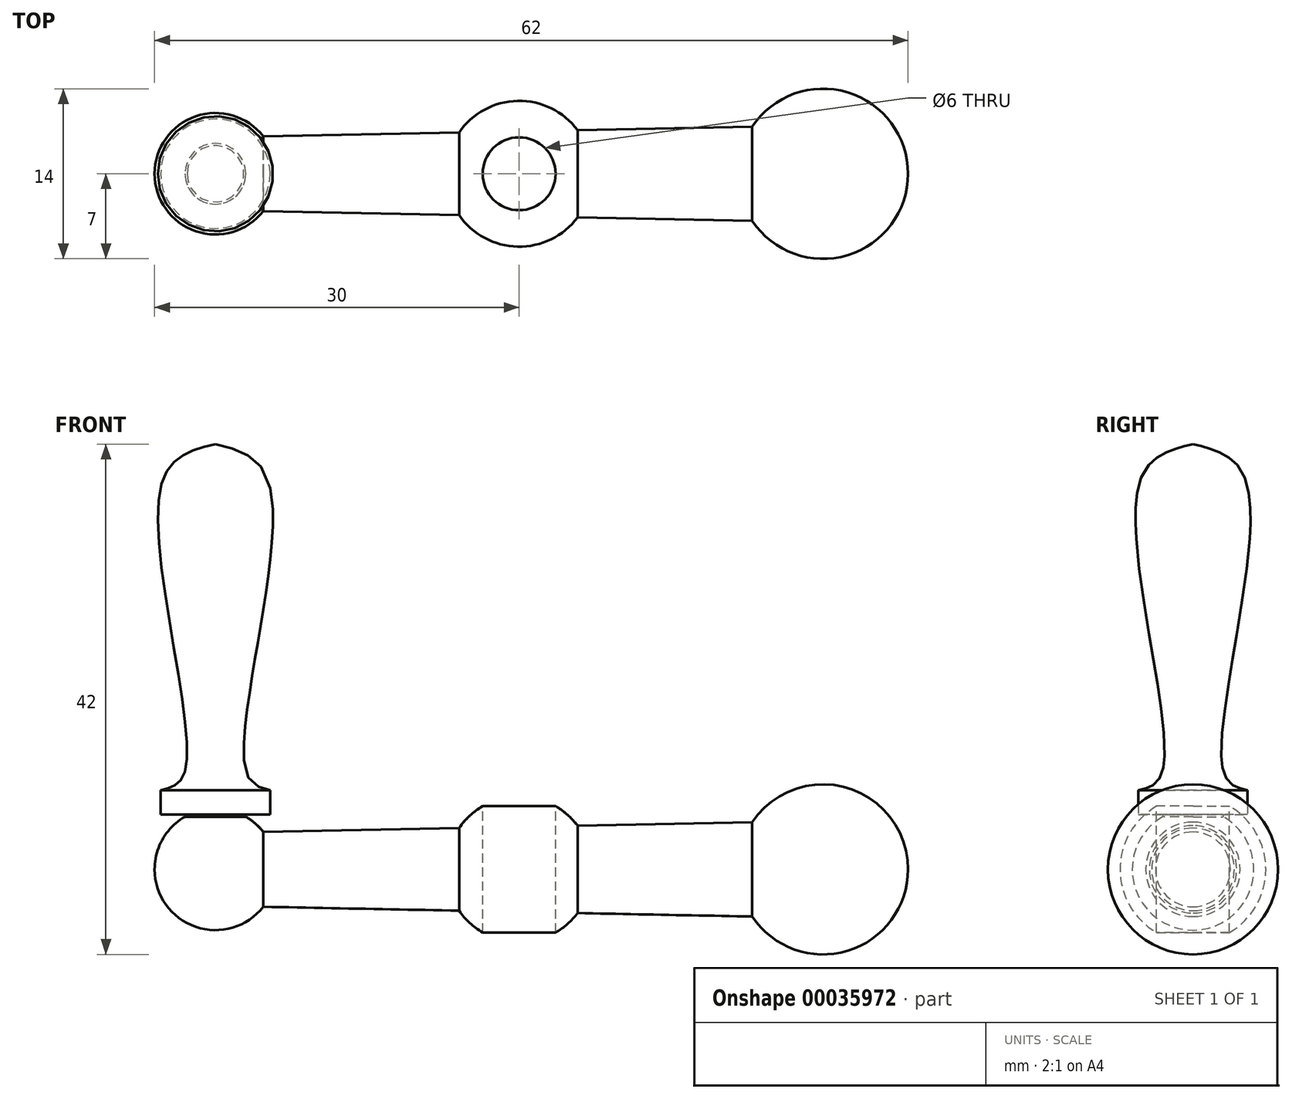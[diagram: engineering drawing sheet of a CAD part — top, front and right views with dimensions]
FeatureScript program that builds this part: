
annotation { "Feature Type Name" : "Feature", "Feature Type Description" : "" }
export const myFeature = defineFeature(function(context is Context, id is Id, definition is map)
    precondition{}
    {
        {
            var Q0;
            Q0=qCreatedBy(makeId("Front.planeOp"),FACE);
            var sketch = newSketch(context, id + "F0", { "sketchPlane" : qUnion([Q0])});
            skArc(sketch, "E0", {"start": v(-6, 0) * mm, "mid": v(0, -6) * mm, "end": v(6, 0) * mm});
            skLineSegment(sketch, "E1", {"start": v(25, 0) * mm, "end": v(0, 0) * mm});
            skLineSegment(sketch, "E2", {"start": v(0, 0) * mm, "end": v(-25, 0) * mm});
            skLineSegment(sketch, "E3", {"start": v(0, 0) * mm, "end": v(25, 0) * mm});
            skArc(sketch, "E4", {"start": v(18, 0) * mm, "mid": v(25, -7) * mm, "end": v(32, 0) * mm});
            skArc(sketch, "E5", {"start": v(-30, 0) * mm, "mid": v(-25, -5) * mm, "end": v(-20, 0) * mm});
            skLineSegment(sketch, "E6", {"start": v(-25, 0) * mm, "end": v(-25, 3) * mm});
            skLineSegment(sketch, "E7", {"start": v(25, 0) * mm, "end": v(25, 4) * mm});
            skLineSegment(sketch, "E8", {"start": v(-25, 3) * mm, "end": v(25, 4) * mm});
            skLineSegment(sketch, "E9", {"start": v(-30, 0) * mm, "end": v(32, 0) * mm});
            skSolve(sketch);
        }
        {
            var Q0;
            {var subQ2=sQuery(id+"F0.wireOp",EDGE,"E6");Q0=makeQuery(id+"F0.imprint","IMPRINT",FACE,{"disambiguationData":[TD([[makeQuery(id+"F0.imprint","IMPRINT",EDGE,{"derivedFrom":subQ2}),-1.0]])]});}
            var Q1;
            Q1=sQuery(id+"F0.wireOp",EDGE,"E9");
            revolve(context, id + "F1", {"entities" : qUnion([Q0]), "axis" : qUnion([Q1]), "revolveType" : RevolveType.FULL});
        }
        {
            var Q0;
            {var subQ0=sQuery(id+"F0.wireOp",EDGE,"E5");Q0=makeQuery(id+"F0.imprint","IMPRINT",FACE,{"disambiguationData":[TD([[makeQuery(id+"F0.imprint","IMPRINT",EDGE,{"derivedFrom":subQ0}),1.0]])]});}
            var Q1;
            {var subQ0=sQuery(id+"F0.wireOp",EDGE,"E0");Q1=makeQuery(id+"F0.imprint","IMPRINT",FACE,{"disambiguationData":[TD([[makeQuery(id+"F0.imprint","IMPRINT",EDGE,{"derivedFrom":subQ0}),1.0]])]});}
            var Q2;
            {var subQ0=sQuery(id+"F0.wireOp",EDGE,"E4");Q2=makeQuery(id+"F0.imprint","IMPRINT",FACE,{"disambiguationData":[TD([[makeQuery(id+"F0.imprint","IMPRINT",EDGE,{"derivedFrom":subQ0}),1.0]])]});}
            var Q3;
            Q3=sQuery(id+"F0.wireOp",EDGE,"E9");
            revolve(context, id + "F2", {"operationType" : NewBodyOperationType.ADD, "entities" : qUnion([Q0, Q1, Q2]), "axis" : qUnion([Q3]), "revolveType" : RevolveType.FULL});
        }
        {
            var Q0;
            Q0=qCreatedBy(makeId("Top.planeOp"),FACE);
            var sketch = newSketch(context, id + "F3", { "sketchPlane" : qUnion([Q0])});
            skCircle(sketch, "E10", {"center": v(0, 0) * mm, "radius": 3 * mm});
            skSolve(sketch);
        }
        {
            var Q0;
            Q0 = qSketchRegion(id + "F3", true);
            extrude(context, id + "F4", {"entities" : qUnion([Q0]), "operationType" : NewBodyOperationType.REMOVE, "oppositeDirection" : true, "depth" : 25 * mm, "hasSecondDirection" : true, "secondDirectionOppositeDirection" : false, "secondDirectionDepth" : 25 * mm});
        }
        {
            var Q0;
            Q0=qCreatedBy(makeId("Front.planeOp"),FACE);
            var sketch = newSketch(context, id + "F5", { "sketchPlane" : qUnion([Q0])});
            skLineSegment(sketch, "E11", {"start": v(-25, 0) * mm, "end": v(-25, 35) * mm});
            skLineSegment(sketch, "E12", {"start": v(-25, 0) * mm, "end": v(-27.5, 0) * mm});
            skLineSegment(sketch, "E13", {"start": v(-27.5, 0) * mm, "end": v(-27.5, 4.5) * mm});
            skLineSegment(sketch, "E14", {"start": v(-27.5, 4.5) * mm, "end": v(-29.5, 4.5) * mm});
            skLineSegment(sketch, "E15", {"start": v(-29.5, 4.5) * mm, "end": v(-29.5, 6.5) * mm});
            skFitSpline(sketch, "E16", {"points": [v(-29.5, 6.5) * mm, v(-27.45, 8.3) * mm, v(-29.5, 31.48) * mm, v(-25, 35) * mm], "startDerivative": vector(14.17, 3.4) * mm, "endDerivative": vector(21.6, 5.15) * mm});
            skSolve(sketch);
        }
        {
            var Q0;
            Q0=makeQuery(id+"F5.imprint","IMPRINT",FACE,{"disambiguationData":[TD([[makeQuery(id+"F5.imprint","IMPRINT",EDGE,{"derivedFrom":sQuery(id+"F5.wireOp",EDGE,"E11")}),1.0]])]});
            var Q1;
            Q1=sQuery(id+"F5.wireOp",EDGE,"E11");
            revolve(context, id + "F6", {"operationType" : NewBodyOperationType.ADD, "entities" : qUnion([Q0]), "axis" : qUnion([Q1]), "revolveType" : RevolveType.FULL});
        }
    });
